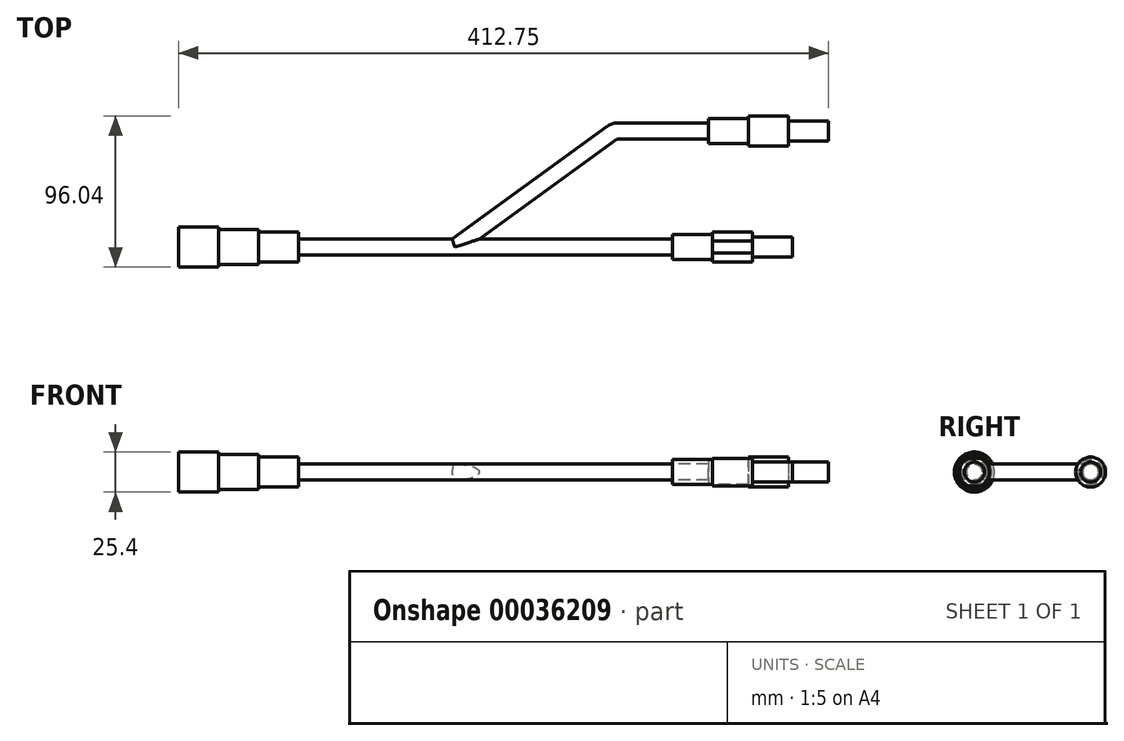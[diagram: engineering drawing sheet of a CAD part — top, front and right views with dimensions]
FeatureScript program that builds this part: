
annotation { "Feature Type Name" : "Feature", "Feature Type Description" : "" }
export const myFeature = defineFeature(function(context is Context, id is Id, definition is map)
    precondition{}
    {
        {
            var Q0;
            Q0=qCreatedBy(makeId("Top.planeOp"),FACE);
            var sketch = newSketch(context, id + "F0", { "sketchPlane" : qUnion([Q0])});
            skLineSegment(sketch, "E0", {"start": v(-287.25, 0) * mm, "end": v(303, 0) * mm, "construction": true});
            skLineSegment(sketch, "E1", {"start": v(-194.87, 0) * mm, "end": v(-194.87, -12.7) * mm});
            skLineSegment(sketch, "E2", {"start": v(194.87, 0) * mm, "end": v(194.87, -6.35) * mm});
            skLineSegment(sketch, "E3", {"start": v(-144.07, -11.11) * mm, "end": v(-144.07, -9.53) * mm});
            skLineSegment(sketch, "E4", {"start": v(-144.07, -9.53) * mm, "end": v(-118.67, -9.53) * mm});
            skLineSegment(sketch, "E5", {"start": v(-118.67, -9.53) * mm, "end": v(-118.67, -5.08) * mm});
            skLineSegment(sketch, "E6", {"start": v(-118.67, -5.08) * mm, "end": v(118.67, -5.08) * mm});
            skLineSegment(sketch, "E7", {"start": v(118.67, -5.08) * mm, "end": v(118.67, -7.94) * mm});
            skLineSegment(sketch, "E8", {"start": v(118.67, -7.94) * mm, "end": v(144.07, -7.94) * mm});
            skLineSegment(sketch, "E9", {"start": v(144.07, -9.53) * mm, "end": v(144.07, -7.94) * mm});
            skLineSegment(sketch, "E10", {"start": v(144.07, -9.53) * mm, "end": v(169.47, -9.53) * mm});
            skLineSegment(sketch, "E11", {"start": v(169.47, -9.53) * mm, "end": v(169.47, -6.35) * mm});
            skLineSegment(sketch, "E12", {"start": v(169.47, -6.35) * mm, "end": v(194.87, -6.35) * mm});
            skLineSegment(sketch, "E13", {"start": v(-194.87, 0) * mm, "end": v(194.87, 0) * mm});
            skLineSegment(sketch, "E14", {"start": v(-19.45, 0) * mm, "end": v(80.48, 72.6) * mm});
            skLineSegment(sketch, "E15", {"start": v(84.22, 73.82) * mm, "end": v(217.88, 73.82) * mm});
            skPoint(sketch, "E16.visualSharp", {"position": v(82.15, 73.82) * mm});
            skArc(sketch, "E16.filletArc", {"start": v(84.22, 73.82) * mm, "mid": v(82.25, 73.5) * mm, "end": v(80.48, 72.6) * mm});
            skLineSegment(sketch, "E17", {"start": v(-144.07, -11.11) * mm, "end": v(-169.47, -11.11) * mm});
            skLineSegment(sketch, "E18", {"start": v(-169.47, -11.11) * mm, "end": v(-169.47, -12.7) * mm});
            skLineSegment(sketch, "E19", {"start": v(-169.47, -12.7) * mm, "end": v(-194.87, -12.7) * mm});
            skSolve(sketch);
        }
        {
            var Q0;
            Q0=makeQuery(id+"F0.imprint","IMPRINT",FACE,{"disambiguationData":[TD([[makeQuery(id+"F0.imprint","IMPRINT",EDGE,{"derivedFrom":sQuery(id+"F0.wireOp",EDGE,"E1")}),1.0]])]});
            var Q1;
            Q1=sQuery(id+"F0.wireOp",EDGE,"E0");
            revolve(context, id + "F1", {"entities" : qUnion([Q0]), "axis" : qUnion([Q1]), "revolveType" : RevolveType.FULL});
        }
        {
            var Q0;
            Q0=qCreatedBy(makeId("Right.planeOp"),FACE);
            var Q1;
            Q1=sQuery(id+"F0.wireOp",VERTEX,"E15.end");
            cPlane(context, id + "F2", {"entities" : qUnion([Q0, Q1]), "cplaneType" : CPlaneType.PLANE_POINT, "offset" : 152.4 * mm, "width" : 152.4 * mm, "height" : 152.4 * mm});
        }
        {
            var Q0;
            Q0=qCreatedBy(id+"F2.planeOp",FACE);
            var sketch = newSketch(context, id + "F3", { "sketchPlane" : qUnion([Q0])});
            skCircle(sketch, "E20", {"center": v(73.82, 0) * mm, "radius": 5.08 * mm});
            skSolve(sketch);
        }
        {
            var Q0;
            Q0=makeQuery(id+"F3.imprint","IMPRINT",FACE,{"disambiguationData":[TD([[makeQuery(id+"F3.imprint","IMPRINT",EDGE,{"derivedFrom":sQuery(id+"F3.wireOp",EDGE,"E20")}),1.0]])]});
            var Q1;
            Q1=sQuery(id+"F0.wireOp",EDGE,"E15");
            var Q2;
            Q2=sQuery(id+"F0.wireOp",EDGE,"E16.filletArc");
            var Q3;
            Q3=sQuery(id+"F0.wireOp",EDGE,"E14");
            sweep(context, id + "F4", {"operationType" : NewBodyOperationType.ADD, "profiles" : qUnion([Q0]), "path" : qUnion([Q1, Q2, Q3])});
        }
        {
            var Q0;
            Q0=qCreatedBy(makeId("Top.planeOp"),FACE);
            var sketch = newSketch(context, id + "F5", { "sketchPlane" : qUnion([Q0])});
            skLineSegment(sketch, "E21", {"start": v(217.88, 73.82) * mm, "end": v(217.88, 80.17) * mm});
            skLineSegment(sketch, "E22", {"start": v(217.88, 80.17) * mm, "end": v(192.48, 80.17) * mm});
            skLineSegment(sketch, "E23", {"start": v(192.48, 83.34) * mm, "end": v(192.48, 80.17) * mm});
            skLineSegment(sketch, "E24", {"start": v(192.48, 83.34) * mm, "end": v(167.08, 83.34) * mm});
            skLineSegment(sketch, "E25", {"start": v(167.08, 83.34) * mm, "end": v(167.08, 81.76) * mm});
            skLineSegment(sketch, "E26", {"start": v(167.08, 81.76) * mm, "end": v(141.68, 81.76) * mm});
            skLineSegment(sketch, "E27", {"start": v(141.68, 81.76) * mm, "end": v(141.68, 73.82) * mm});
            skLineSegment(sketch, "E28", {"start": v(141.68, 73.82) * mm, "end": v(217.88, 73.82) * mm});
            skLineSegment(sketch, "E29", {"start": v(79.02, 73.82) * mm, "end": v(347.98, 73.82) * mm, "construction": true});
            skSolve(sketch);
        }
        {
            var Q0;
            Q0=makeQuery(id+"F5.imprint","IMPRINT",FACE,{"disambiguationData":[TD([[makeQuery(id+"F5.imprint","IMPRINT",EDGE,{"derivedFrom":sQuery(id+"F5.wireOp",EDGE,"E21")}),1.0]])]});
            var Q1;
            Q1=sQuery(id+"F5.wireOp",EDGE,"E29");
            revolve(context, id + "F6", {"operationType" : NewBodyOperationType.ADD, "entities" : qUnion([Q0]), "axis" : qUnion([Q1]), "revolveType" : RevolveType.FULL});
        }
        {
            var Q0;
            Q0=qCreatedBy(makeId("Right.planeOp"),FACE);
            var sketch = newSketch(context, id + "F7", { "sketchPlane" : qUnion([Q0])});
            skLineSegment(sketch, "E30.bottom", {"start": v(-3.81, 9.53) * mm, "end": v(3.81, 9.53) * mm});
            skLineSegment(sketch, "E30.top", {"start": v(-3.81, 8.73) * mm, "end": v(3.81, 8.73) * mm});
            skLineSegment(sketch, "E30.left", {"start": v(-3.81, 9.53) * mm, "end": v(-3.81, 8.73) * mm});
            skLineSegment(sketch, "E30.right", {"start": v(3.81, 9.53) * mm, "end": v(3.81, 8.73) * mm});
            skLineSegment(sketch, "E31.MirrorCS", {"start": v(-3.81, -8.73) * mm, "end": v(3.81, -8.73) * mm});
            skLineSegment(sketch, "E32.MirrorCS", {"start": v(-3.81, -9.53) * mm, "end": v(3.81, -9.53) * mm});
            skLineSegment(sketch, "E33.MirrorCS", {"start": v(-3.81, -9.53) * mm, "end": v(-3.81, -8.73) * mm});
            skLineSegment(sketch, "E34.MirrorCS", {"start": v(3.81, -9.53) * mm, "end": v(3.81, -8.73) * mm});
            skSolve(sketch);
        }
        {
            var Q0;
            Q0 = qSketchRegion(id + "F7", true);
            extrude(context, id + "F8", {"entities" : qUnion([Q0]), "operationType" : NewBodyOperationType.REMOVE, "endBound" : BoundingType.THROUGH_ALL, "depth" : 25.4 * mm});
        }
    });
